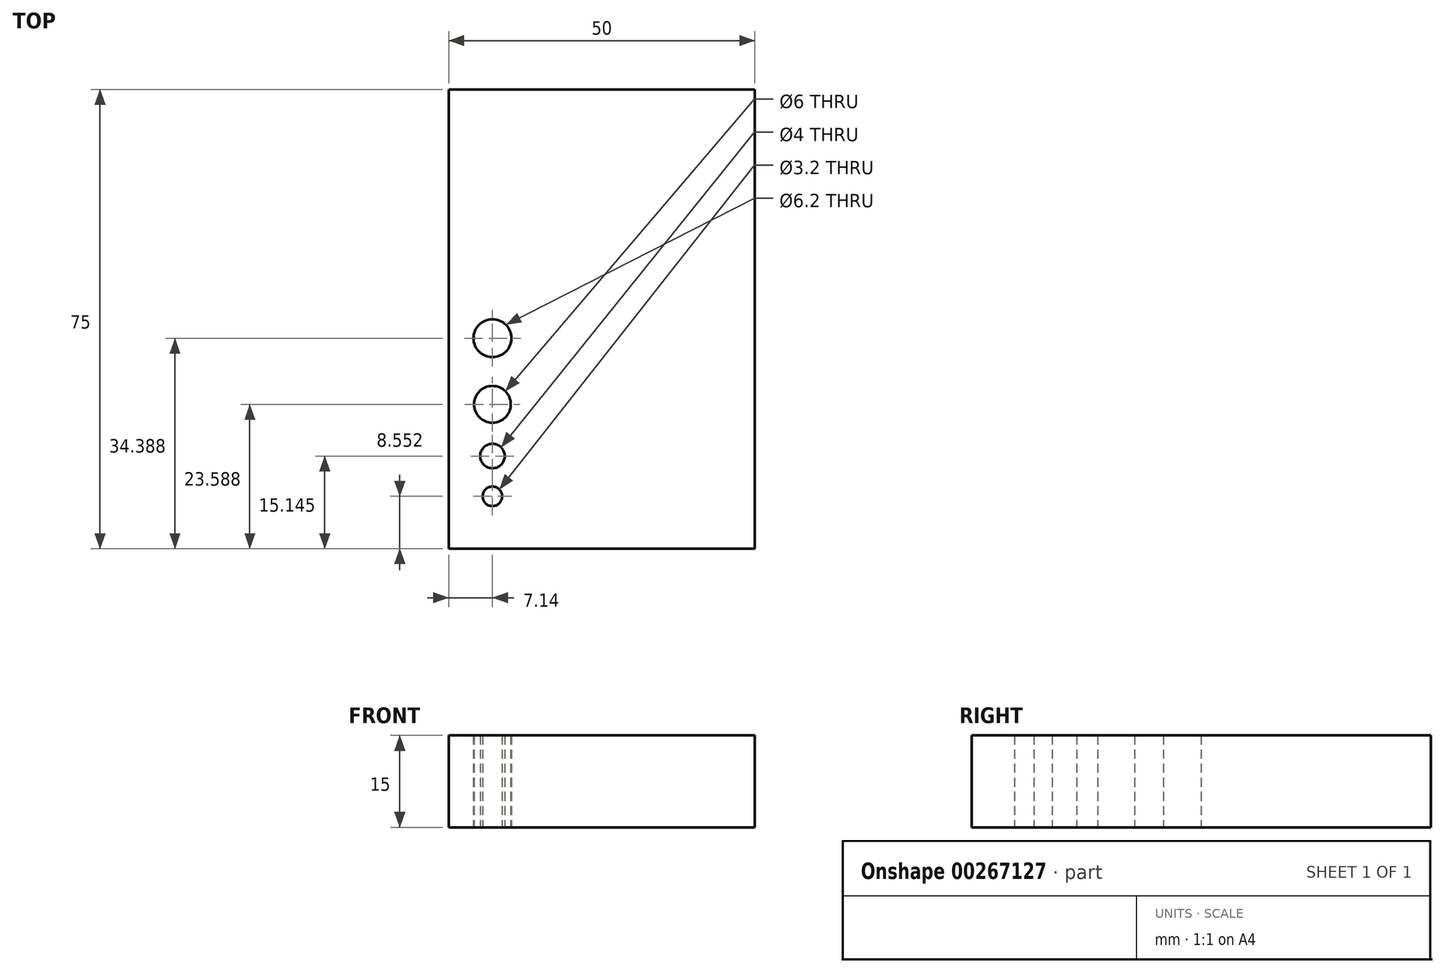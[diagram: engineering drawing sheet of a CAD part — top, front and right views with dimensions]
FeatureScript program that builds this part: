
annotation { "Feature Type Name" : "Feature", "Feature Type Description" : "" }
export const myFeature = defineFeature(function(context is Context, id is Id, definition is map)
    precondition{}
    {
        {
            var Q0;
            Q0=qCreatedBy(makeId("Top.planeOp"),FACE);
            var sketch = newSketch(context, id + "F0", { "sketchPlane" : qUnion([Q0])});
            skLineSegment(sketch, "E0.bottom", {"start": v(0, 0) * mm, "end": v(50, 0) * mm});
            skLineSegment(sketch, "E0.top", {"start": v(0, 75) * mm, "end": v(50, 75) * mm});
            skLineSegment(sketch, "E0.left", {"start": v(0, 0) * mm, "end": v(0, 75) * mm});
            skLineSegment(sketch, "E0.right", {"start": v(50, 0) * mm, "end": v(50, 75) * mm});
            skCircle(sketch, "E1", {"center": v(7.14, 8.55) * mm, "radius": 1.6 * mm});
            skCircle(sketch, "E2", {"center": v(7.14, 15.15) * mm, "radius": 2 * mm});
            skCircle(sketch, "E3", {"center": v(7.14, 23.59) * mm, "radius": 3 * mm});
            skCircle(sketch, "E4", {"center": v(7.14, 34.39) * mm, "radius": 3.1 * mm});
            skSolve(sketch);
        }
        {
            var Q0;
            Q0=makeQuery(id+"F0.imprint","IMPRINT",FACE,{"disambiguationData":[TD([[makeQuery(id+"F0.imprint","IMPRINT",EDGE,{"derivedFrom":sQuery(id+"F0.wireOp",EDGE,"E0.bottom")}),1.0]])]});
            extrude(context, id + "F1", {"entities" : qUnion([Q0]), "depth" : 15 * mm});
        }
    });
